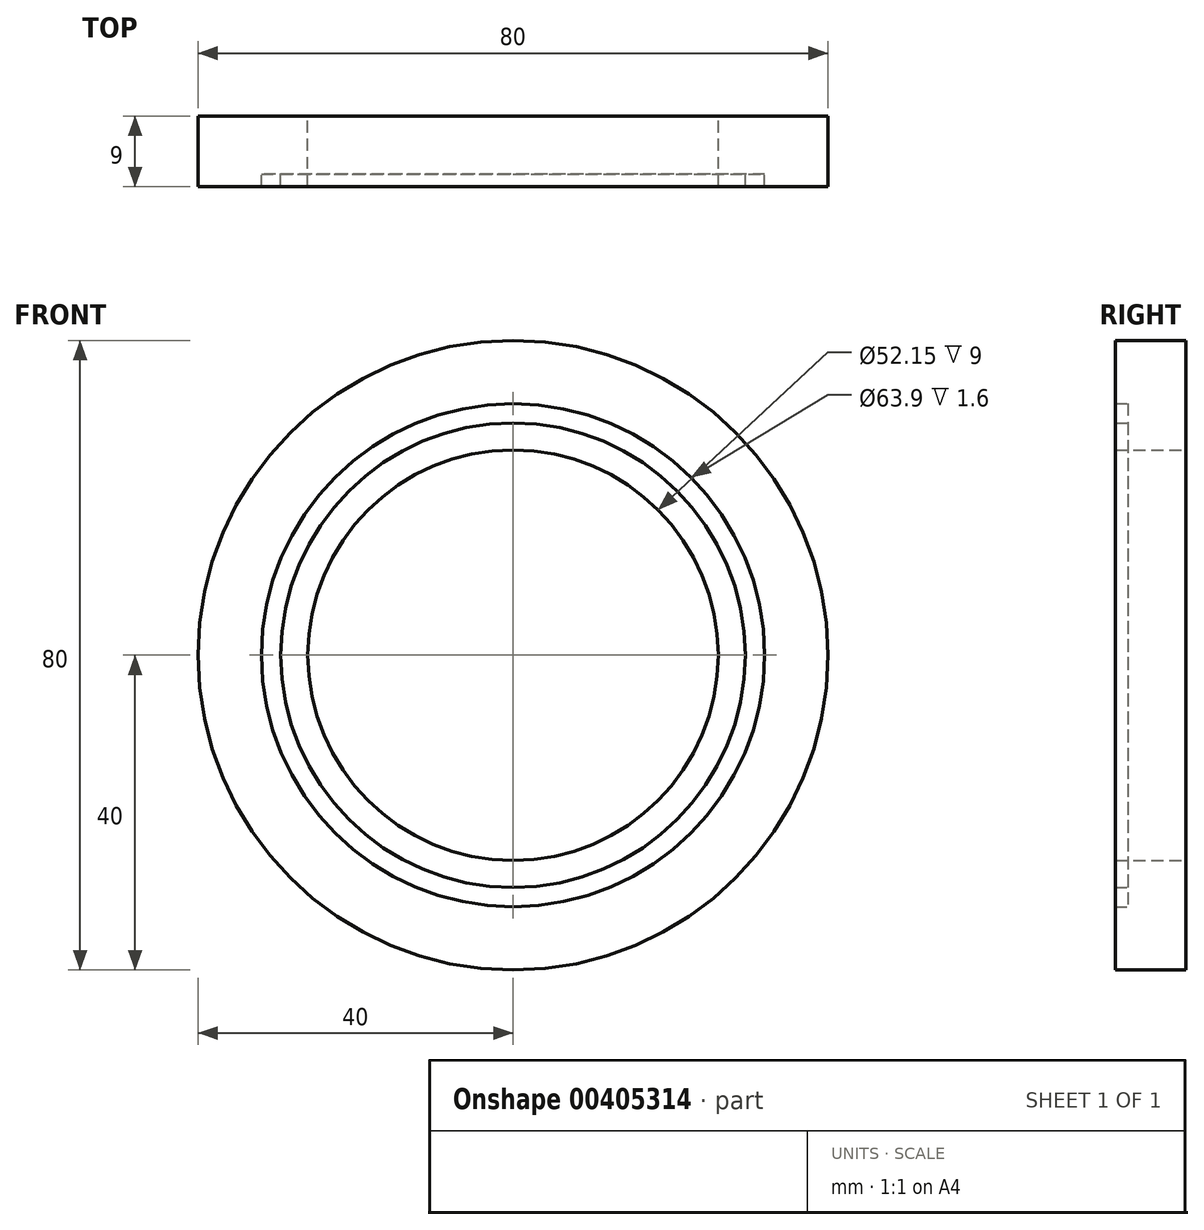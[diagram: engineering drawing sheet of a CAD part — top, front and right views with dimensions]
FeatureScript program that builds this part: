
annotation { "Feature Type Name" : "Feature", "Feature Type Description" : "" }
export const myFeature = defineFeature(function(context is Context, id is Id, definition is map)
    precondition{}
    {
        {
            var Q0;
            Q0=qCreatedBy(makeId("Front.planeOp"),FACE);
            var sketch = newSketch(context, id + "F0", { "sketchPlane" : qUnion([Q0])});
            skCircle(sketch, "E0", {"center": v(0, 0) * mm, "radius": 26.07 * mm});
            skCircle(sketch, "E1", {"center": v(0, 0) * mm, "radius": 40 * mm});
            skSolve(sketch);
        }
        {
            var Q0;
            Q0=makeQuery(id+"F0.imprint","IMPRINT",FACE,{"disambiguationData":[TD([[makeQuery(id+"F0.imprint","IMPRINT",EDGE,{"derivedFrom":sQuery(id+"F0.wireOp",EDGE,"E0")}),-1.0]])]});
            extrude(context, id + "F1", {"entities" : qUnion([Q0]), "depth" : 9 * mm});
        }
        {
            var Q0;
            Q0=qCreatedBy(makeId("Right.planeOp"),FACE);
            var sketch = newSketch(context, id + "F2", { "sketchPlane" : qUnion([Q0])});
            skLineSegment(sketch, "E2.bottom", {"start": v(-9, -29.5) * mm, "end": v(-7.4, -29.5) * mm});
            skLineSegment(sketch, "E2.top", {"start": v(-9, -31.95) * mm, "end": v(-7.4, -31.95) * mm});
            skLineSegment(sketch, "E2.left", {"start": v(-9, -29.5) * mm, "end": v(-9, -31.95) * mm});
            skLineSegment(sketch, "E2.right", {"start": v(-7.4, -29.5) * mm, "end": v(-7.4, -31.95) * mm});
            skLineSegment(sketch, "E3", {"start": v(-9, -29.5) * mm, "end": v(-9, 0) * mm});
            skLineSegment(sketch, "E4", {"start": v(-7.4, -31.95) * mm, "end": v(-7.4, 0) * mm});
            skSolve(sketch);
        }
        {
            var Q0;
            Q0 = qSketchRegion(id + "F2", true);
            var Q1;
            Q1=makeQuery(id+"F1.opExtrude","SWEPT_FACE",FACE,{"disambiguationData":[OSD([sQuery(id+"F0.wireOp",EDGE,"E1")])]});
            revolve(context, id + "F3", {"operationType" : NewBodyOperationType.REMOVE, "entities" : qUnion([Q0]), "axis" : qUnion([Q1]), "revolveType" : RevolveType.FULL, "oppositeDirection" : true});
        }
    });
